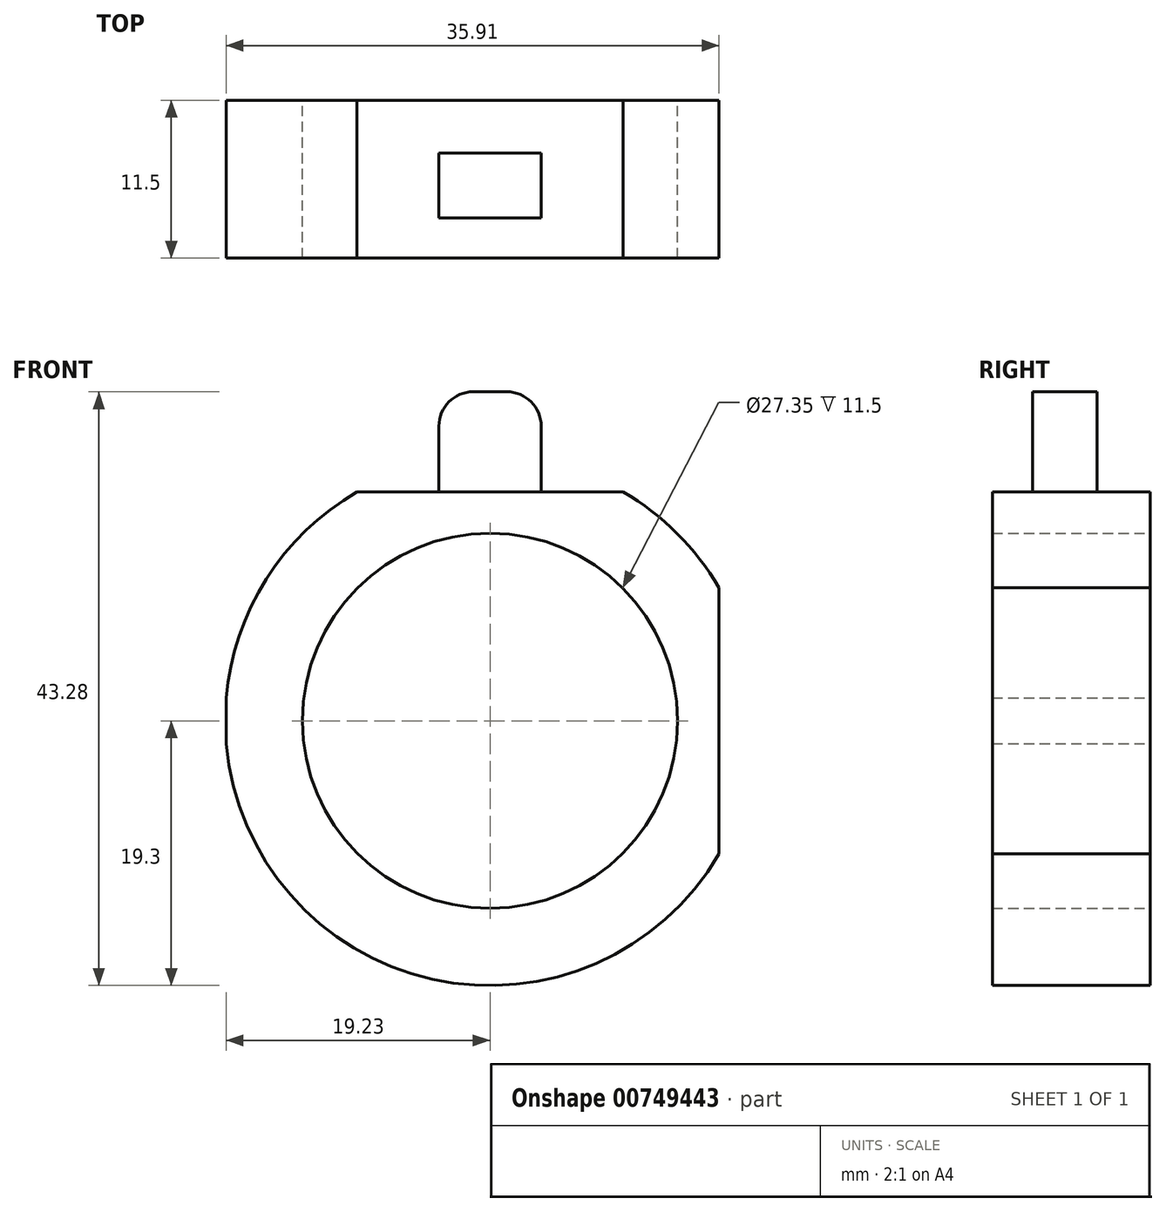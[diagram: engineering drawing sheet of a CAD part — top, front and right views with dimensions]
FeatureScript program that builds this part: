
annotation { "Feature Type Name" : "Feature", "Feature Type Description" : "" }
export const myFeature = defineFeature(function(context is Context, id is Id, definition is map)
    precondition{}
    {
        {
            var Q0;
            Q0=qCreatedBy(makeId("Front.planeOp"),FACE);
            var sketch = newSketch(context, id + "F0", { "sketchPlane" : qUnion([Q0])});
            skCircle(sketch, "E0", {"center": v(0, 0) * mm, "radius": 13.67 * mm});
            skArc(sketch, "E1", {"start": v(-19.23, -1.66) * mm, "mid": v(-4.22, -18.83) * mm, "end": v(16.68, -9.7) * mm});
            skPoint(sketch, "E2.middle", {"position": v(-30.15, 0) * mm});
            skArc(sketch, "E3.trimOffspring", {"start": v(16.68, 9.7) * mm, "mid": v(13.65, 13.65) * mm, "end": v(9.7, 16.68) * mm});
            skLineSegment(sketch, "E4", {"start": v(-19.23, 1.66) * mm, "end": v(-19.23, -1.66) * mm});
            skLineSegment(sketch, "E5", {"start": v(-9.7, 16.68) * mm, "end": v(9.7, 16.68) * mm});
            skLineSegment(sketch, "E6.1.0", {"start": v(16.68, 9.7) * mm, "end": v(16.68, -9.7) * mm});
            skLineSegment(sketch, "E6.anchor1", {"start": v(0, 0) * mm, "end": v(-9.7, 16.68) * mm, "construction": true});
            skLineSegment(sketch, "E6.anchor2", {"start": v(0, 0) * mm, "end": v(16.68, 9.7) * mm, "construction": true});
            skArc(sketch, "E7.trimOffspring", {"start": v(-9.7, 16.68) * mm, "mid": v(-16.3, 10.33) * mm, "end": v(-19.23, 1.66) * mm});
            skPoint(sketch, "E8.orphan", {"position": v(19.23, -1.66) * mm});
            skPoint(sketch, "E9.orphan", {"position": v(19.23, 1.66) * mm});
            skSolve(sketch);
        }
        {
            var Q0;
            Q0 = qSketchRegion(id + "F0", true);
            extrude(context, id + "F1", {"entities" : qUnion([Q0]), "depth" : 11.5 * mm, "offsetDistance" : 25 * mm});
        }
        {
            var Q0;
            Q0=makeQuery(id+"F1.opExtrude","SWEPT_FACE",FACE,{"disambiguationData":[OSD([sQuery(id+"F0.wireOp",EDGE,"E5")])]});
            var sketch = newSketch(context, id + "F2", { "sketchPlane" : qUnion([Q0])});
            skLineSegment(sketch, "E10.bottom", {"start": v(3.73, -8.57) * mm, "end": v(-3.73, -8.57) * mm});
            skLineSegment(sketch, "E10.top", {"start": v(3.73, -3.86) * mm, "end": v(-3.73, -3.86) * mm});
            skLineSegment(sketch, "E10.left", {"start": v(3.73, -8.57) * mm, "end": v(3.73, -3.86) * mm});
            skLineSegment(sketch, "E10.right", {"start": v(-3.73, -8.57) * mm, "end": v(-3.73, -3.86) * mm});
            skPoint(sketch, "E10.middle", {"position": v(0, -6.21) * mm});
            skSolve(sketch);
        }
        {
            var Q0;
            Q0 = qSketchRegion(id + "F2", true);
            extrude(context, id + "F3", {"entities" : qUnion([Q0]), "operationType" : NewBodyOperationType.ADD, "depth" : 7.3 * mm, "offsetDistance" : 25 * mm});
        }
        {
            var Q0;
            Q0=makeQuery(id+"F3.opExtrude","CAP_EDGE",EDGE,{"disambiguationData":[OSD([sQuery(id+"F2.wireOp",EDGE,"E10.right")])],"isStart":false});
            var Q1;
            Q1=makeQuery(id+"F3.opExtrude","CAP_EDGE",EDGE,{"disambiguationData":[OSD([sQuery(id+"F2.wireOp",EDGE,"E10.left")])],"isStart":false});
            var Q2;
            Q2=makeQuery(id+"F3.opExtrude","CAP_EDGE",EDGE,{"disambiguationData":[OSD([sQuery(id+"F2.wireOp",EDGE,"E10.left")])],"isStart":true});
            var Q3;
            Q3=makeQuery(id+"F3.opExtrude","CAP_EDGE",EDGE,{"disambiguationData":[OSD([sQuery(id+"F2.wireOp",EDGE,"E10.right")])],"isStart":true});
            fillet(context, id + "F4", {"entities" : qUnion([Q0, Q1, Q2, Q3]), "radius" : 2.5 * mm, "tangentPropagation" : true, "allowEdgeOverflow" : false});
        }
    });
